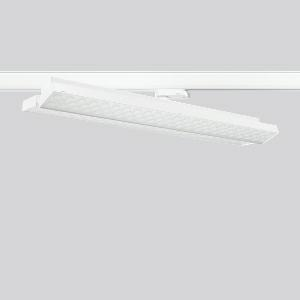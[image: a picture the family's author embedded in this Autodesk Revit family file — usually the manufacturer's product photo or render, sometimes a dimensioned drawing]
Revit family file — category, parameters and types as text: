
# Revit family: tx-move_742163_002_2_76_be07
name_source: partatom
category: Lighting Fixtures
units: mm (PartAtom-declared; Revit-internal decimal feet)

## family parameters
Cut with Voids When Loaded = No
Host = Face
Light Source = No
Part Type = Normal
Room Calculation Point = No
Round Connector Dimension = Use Diameter
Shared = No

## types (1)
- MultiLumen 1 (1 x LED Modul 927, 1975 lm, 2700)
    Apparent Load = 38 VA
    CIE Flux Codes = 65 90 98 100 100
    Color Rendering = 92
    Color Temperature = 2700
    Default Elevation = 1800 mm
    Description = Series: TX-MOVE
Multifunctional surface-mounted spotlight for area lighting. Very flat design. Housing: sheet steel, powder-coated. Rotation range: 356°. Swivel range: 90°. Consistent alignment possible with visible tilt scale. High-efficiency LED units with optimum light control thanks to clear plastic (PC) lens optics. Spezielle Mikrostrukturen reduzieren Gelbsaum. Asymmetrical light distribution. Best colour rendering with CRI >90 for fresh products and coloured textiles. With adapter for RZB 3-circuit DALI tracks. Suitable for Track on ceiling. MultiLumen: Luminous flux adjustable in 3 steps. Factory setting is the highest luminous flux. Environmentally friendly and resource-saving due to replaceable and recyclable components. 
Colour: traffic white, matt (RAL 9016)
Length: 570 mm
Width: 119 mm
Height: 88 mm
Lamp: LED
Socket: without socket
Colour temperature: 2700K
Colour rendering index (CRI): 90
System power: 38 W
Rated luminous flux: 3950 lm
Luminous efficiency: 104 lm/W
System power 2: 51 W
Rated luminous flux 2: 5150 lm
Luminous efficiency 2: 101 lm/W
System power 3: 62 W
Rated luminous flux 3: 6150 lm
Luminous efficiency 3: 99 lm/W
Control gear: Dimmable EVG, DALI
Protection class: I
Type of protection: IP 20
    Height = 75 mm
    Lamp = 1 x LED Modul 927
    Lamp Light Flux = 1975 lm
    Lamp count = 1
    Length = 569 mm
    Lifetime = 50000 h
    Luminous efficacy = 104 lm/W
    Manufacturer = RZB
    ModVariant = No
    Model = 742163.002.2.76
    Mounting Place = Ceiling
    Mounting Type = Surface mounted
    Number of Poles = 1
    OnlyDefault = Yes
    Power Factor = 1
    Product Name = TX-MOVE
    Product group = Track mounted projectors
    ProductGroupID = 301
    Protection Class = Protection class I
    Protection Degree = IP 20
    RLX_Detail_Level = 1
    RLX_Emergency_Light_Flux = 0 lm
    RLX_Emergency_Type = 0
    RLX_Emergency_Type_DB = No
    RlxData = <blob elided: 51677 chars, md5=ace9ec72>
    Socket = socket
    Standby Power = 0 W
    System Light Flux = 3950 lm
    System Power = 38 W
    Type Comments = MultiLumen 1
    Type Image = 742162.002.jpg
    URL = http://relux.com
    VarID = multilumen_1
    Voltage = 0 V
    Weight = 0.00 kg
    Width = 119 mm

## geometry (parser evidence)
native form markers: Blend x4, Sweep x14
no freeform markers — native parametric forms only
